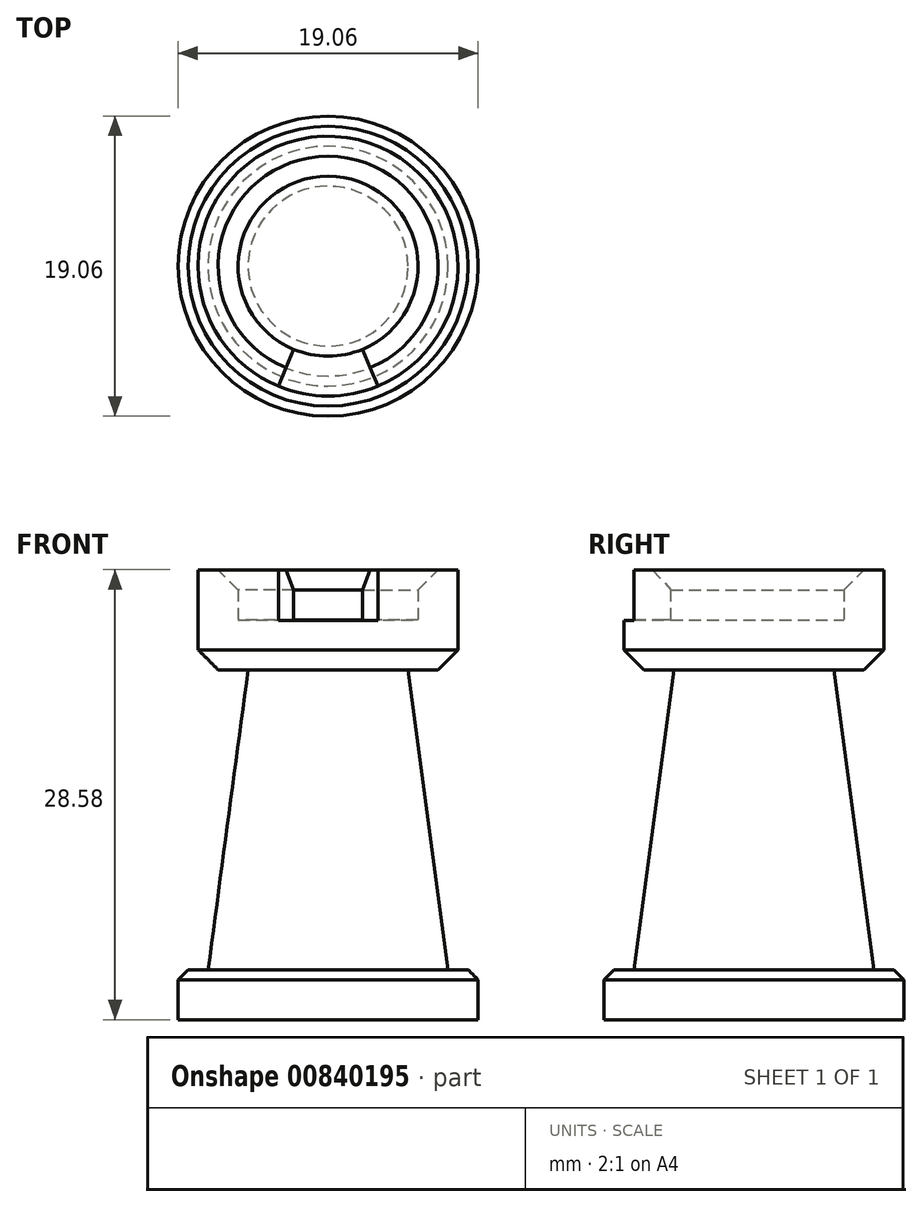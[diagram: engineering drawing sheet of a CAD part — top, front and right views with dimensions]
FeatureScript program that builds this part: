
annotation { "Feature Type Name" : "Feature", "Feature Type Description" : "" }
export const myFeature = defineFeature(function(context is Context, id is Id, definition is map)
    precondition{}
    {
        {
            var Q0;
            Q0=qCreatedBy(makeId("Top.planeOp"),FACE);
            var sketch = newSketch(context, id + "F0", { "sketchPlane" : qUnion([Q0])});
            skCircle(sketch, "E0", {"center": v(0, 0) * mm, "radius": 9.53 * mm});
            skSolve(sketch);
        }
        {
            var Q0;
            Q0 = qSketchRegion(id + "F0", true);
            extrude(context, id + "F1", {"entities" : qUnion([Q0]), "depth" : 3.17 * mm, "offsetDistance" : 25.4 * mm});
        }
        {
            var Q0;
            Q0=makeQuery(id+"F1.opExtrude","CAP_EDGE",EDGE,{"disambiguationData":[OSD([sQuery(id+"F0.wireOp",EDGE,"E0")])],"isStart":false});
            chamfer(context, id + "F2", {"entities" : qUnion([Q0]), "width" : 0.64 * mm, "tangentPropagation" : true});
        }
        {
            var Q0;
            Q0=qCreatedBy(makeId("Front.planeOp"),FACE);
            var sketch = newSketch(context, id + "F3", { "sketchPlane" : qUnion([Q0])});
            skLineSegment(sketch, "E1", {"start": v(0, 9.21) * mm, "end": v(0, 3.18) * mm, "construction": true});
            skLineSegment(sketch, "E2", {"start": v(-7.62, 3.18) * mm, "end": v(0, 3.18) * mm});
            skLineSegment(sketch, "E3", {"start": v(0, 3.18) * mm, "end": v(0, 22.23) * mm});
            skLineSegment(sketch, "E4", {"start": v(-7.62, 3.18) * mm, "end": v(-5.08, 22.23) * mm});
            skLineSegment(sketch, "E5", {"start": v(9.53, 0) * mm, "end": v(-9.53, 0) * mm, "construction": true});
            skLineSegment(sketch, "E6", {"start": v(-5.08, 22.23) * mm, "end": v(-8.26, 22.23) * mm});
            skLineSegment(sketch, "E7", {"start": v(-8.26, 22.23) * mm, "end": v(-8.26, 28.58) * mm});
            skLineSegment(sketch, "E8", {"start": v(-8.26, 28.58) * mm, "end": v(-5.72, 28.58) * mm});
            skLineSegment(sketch, "E9", {"start": v(-5.72, 28.58) * mm, "end": v(-5.72, 25.4) * mm});
            skLineSegment(sketch, "E10", {"start": v(-5.72, 25.4) * mm, "end": v(0, 25.4) * mm});
            skLineSegment(sketch, "E11", {"start": v(0, 25.4) * mm, "end": v(0, 22.23) * mm});
            skSolve(sketch);
        }
        {
            var Q0;
            Q0 = qSketchRegion(id + "F3", true);
            var Q1;
            Q1=sQuery(id+"F3.wireOp",EDGE,"E3");
            revolve(context, id + "F4", {"operationType" : NewBodyOperationType.ADD, "surfaceOperationType" : NewSurfaceOperationType.NEW, "entities" : qUnion([Q0]), "axis" : qUnion([Q1]), "revolveType" : RevolveType.FULL});
        }
        {
            var Q0;
            Q0=qCreatedBy(makeId("Right.planeOp"),FACE);
            var sketch = newSketch(context, id + "F5", { "sketchPlane" : qUnion([Q0])});
            skLineSegment(sketch, "E12", {"start": v(-5.72, 28.58) * mm, "end": v(-8.26, 28.58) * mm});
            skLineSegment(sketch, "E13", {"start": v(-5.72, 25.4) * mm, "end": v(-5.72, 28.58) * mm});
            skLineSegment(sketch, "E14", {"start": v(-8.26, 25.37) * mm, "end": v(-8.26, 28.58) * mm});
            skLineSegment(sketch, "E15", {"start": v(-5.72, 28.58) * mm, "end": v(-5.72, 25.4) * mm});
            skLineSegment(sketch, "E16", {"start": v(-8.26, 28.58) * mm, "end": v(-8.26, 25.37) * mm});
            skLineSegment(sketch, "E17", {"start": v(-8.26, 25.37) * mm, "end": v(-5.72, 25.4) * mm});
            skPoint(sketch, "E18.end.orphan", {"position": v(-7.62, 3.17) * mm});
            skPoint(sketch, "E18.start.orphan", {"position": v(-5.08, 22.23) * mm});
            skPoint(sketch, "E19.start.orphan", {"position": v(-8.26, 22.23) * mm});
            skPoint(sketch, "E20.end.orphan", {"position": v(5.08, 22.23) * mm});
            skPoint(sketch, "E20.start.orphan", {"position": v(7.62, 3.17) * mm});
            skPoint(sketch, "E21.end.orphan", {"position": v(8.26, 22.23) * mm});
            skPoint(sketch, "E22.end.orphan", {"position": v(8.26, 28.58) * mm});
            skPoint(sketch, "E23.end.orphan", {"position": v(5.72, 28.58) * mm});
            skPoint(sketch, "E24.end.orphan", {"position": v(5.72, 25.4) * mm});
            skSolve(sketch);
        }
        {
            var Q0;
            Q0 = qSketchRegion(id + "F5", true);
            var Q1;
            Q1=sQuery(id+"F3.wireOp",EDGE,"E3");
            revolve(context, id + "F6", {"operationType" : NewBodyOperationType.REMOVE, "surfaceOperationType" : NewSurfaceOperationType.NEW, "entities" : qUnion([Q0]), "axis" : qUnion([Q1]), "revolveType" : RevolveType.SYMMETRIC, "oppositeDirection" : true, "angle" : 45 * degree});
        }
        {
            var Q0;
            Q0=makeQuery(id+"F4.opRevolve","SWEPT_EDGE",EDGE,{"disambiguationData":[OSD([sQuery(id+"F3.wireOp",EDGE,"E6"),sQuery(id+"F3.wireOp",EDGE,"E7")])]});
            chamfer(context, id + "F7", {"entities" : qUnion([Q0]), "width" : 1.27 * mm, "tangentPropagation" : true});
        }
        {
            var Q0;
            {var subQ0=sQuery(id+"F3.wireOp",EDGE,"E8");var subQ1=sQuery(id+"F3.wireOp",EDGE,"E9");var subQ2=sQuery(id+"F5.wireOp",EDGE,"E17");var subQ3=sQuery(id+"F5.wireOp",EDGE,"E16");var subQ4=sQuery(id+"F5.wireOp",EDGE,"E15");var subQ5=sQuery(id+"F5.wireOp",EDGE,"E12");Q0=makeQuery(id+"FbDiJmaGxYr5mtq_1.1.F6.boolean.opBoolean","SPLIT",EDGE,{"disambiguationData":[TD([makeQuery(id+"F6.boolean.opBoolean","COPY",FACE,{"derivedFrom":makeQuery(id+"F6.opRevolve","CAP_FACE",FACE,{"disambiguationData":[OSD([subQ5,subQ4,subQ3,subQ2])],"isStart":false})})])],"derivedFrom":makeQuery(id+"F4.opRevolve","SWEPT_EDGE",EDGE,{"disambiguationData":[OSD([subQ0,subQ1])]})});}
            var Q1;
            {var subQ0=sQuery(id+"F3.wireOp",EDGE,"E8");var subQ2=sQuery(id+"F5.wireOp",EDGE,"E17");var subQ3=sQuery(id+"F5.wireOp",EDGE,"E16");var subQ4=sQuery(id+"F5.wireOp",EDGE,"E15");var subQ5=sQuery(id+"F5.wireOp",EDGE,"E12");var subQ6=makeQuery(id+"FbDiJmaGxYr5mtq_1.1.F6.opRevolve","CAP_FACE",FACE,{"disambiguationData":[OSD([subQ5,subQ4,subQ3,subQ2])],"isStart":false});var subQ7=sQuery(id+"F3.wireOp",EDGE,"E9");Q1=makeQuery(id+"FbDiJmaGxYr5mtq_1.2.F6.boolean.opBoolean","SPLIT",EDGE,{"disambiguationData":[TD([makeQuery(id+"FbDiJmaGxYr5mtq_1.1.F6.boolean.opBoolean","COPY",FACE,{"derivedFrom":subQ6})])],"derivedFrom":makeQuery(id+"FbDiJmaGxYr5mtq_1.1.F6.boolean.opBoolean","SPLIT",EDGE,{"disambiguationData":[TD([makeQuery(id+"F6.boolean.opBoolean","COPY",FACE,{"derivedFrom":makeQuery(id+"F6.opRevolve","CAP_FACE",FACE,{"disambiguationData":[OSD([subQ5,subQ4,subQ3,subQ2])],"isStart":true})})])],"derivedFrom":makeQuery(id+"F4.opRevolve","SWEPT_EDGE",EDGE,{"disambiguationData":[OSD([subQ0,subQ7])]})})});}
            var Q2;
            {var subQ0=sQuery(id+"F3.wireOp",EDGE,"E8");var subQ2=sQuery(id+"F3.wireOp",EDGE,"E9");var subQ4=sQuery(id+"F5.wireOp",EDGE,"E17");var subQ5=sQuery(id+"F5.wireOp",EDGE,"E16");var subQ6=sQuery(id+"F5.wireOp",EDGE,"E15");var subQ7=sQuery(id+"F5.wireOp",EDGE,"E12");var subQ8=makeQuery(id+"FbDiJmaGxYr5mtq_1.2.F6.opRevolve","CAP_FACE",FACE,{"disambiguationData":[OSD([subQ7,subQ6,subQ5,subQ4])],"isStart":false});var subQ9=makeQuery(id+"F6.boolean.opBoolean","COPY",FACE,{"derivedFrom":makeQuery(id+"F6.opRevolve","CAP_FACE",FACE,{"disambiguationData":[OSD([subQ7,subQ6,subQ5,subQ4])],"isStart":true})});Q2=makeQuery(id+"FbDiJmaGxYr5mtq_1.3.F6.boolean.opBoolean","SPLIT",EDGE,{"disambiguationData":[TD([makeQuery(id+"FbDiJmaGxYr5mtq_1.2.F6.boolean.opBoolean","COPY",FACE,{"derivedFrom":subQ8})])],"derivedFrom":makeQuery(id+"FbDiJmaGxYr5mtq_1.2.F6.boolean.opBoolean","SPLIT",EDGE,{"disambiguationData":[TD([subQ9])],"derivedFrom":makeQuery(id+"FbDiJmaGxYr5mtq_1.1.F6.boolean.opBoolean","SPLIT",EDGE,{"disambiguationData":[TD([subQ9])],"derivedFrom":makeQuery(id+"F4.opRevolve","SWEPT_EDGE",EDGE,{"disambiguationData":[OSD([subQ0,subQ2])]})})})});}
            var Q3;
            {var subQ0=sQuery(id+"F3.wireOp",EDGE,"E8");var subQ2=sQuery(id+"F5.wireOp",EDGE,"E17");var subQ3=sQuery(id+"F5.wireOp",EDGE,"E16");var subQ4=sQuery(id+"F5.wireOp",EDGE,"E15");var subQ5=sQuery(id+"F5.wireOp",EDGE,"E12");var subQ6=sQuery(id+"F3.wireOp",EDGE,"E9");var subQ8=makeQuery(id+"F6.boolean.opBoolean","COPY",FACE,{"derivedFrom":makeQuery(id+"F6.opRevolve","CAP_FACE",FACE,{"disambiguationData":[OSD([subQ5,subQ4,subQ3,subQ2])],"isStart":true})});Q3=makeQuery(id+"FbDiJmaGxYr5mtq_1.3.F6.boolean.opBoolean","SPLIT",EDGE,{"disambiguationData":[TD([subQ8])],"derivedFrom":makeQuery(id+"FbDiJmaGxYr5mtq_1.2.F6.boolean.opBoolean","SPLIT",EDGE,{"disambiguationData":[TD([subQ8])],"derivedFrom":makeQuery(id+"FbDiJmaGxYr5mtq_1.1.F6.boolean.opBoolean","SPLIT",EDGE,{"disambiguationData":[TD([subQ8])],"derivedFrom":makeQuery(id+"F4.opRevolve","SWEPT_EDGE",EDGE,{"disambiguationData":[OSD([subQ0,subQ6])]})})})});}
            chamfer(context, id + "F8", {"entities" : qUnion([Q0, Q1, Q2, Q3]), "width" : 1.27 * mm, "tangentPropagation" : true});
        }
    });
